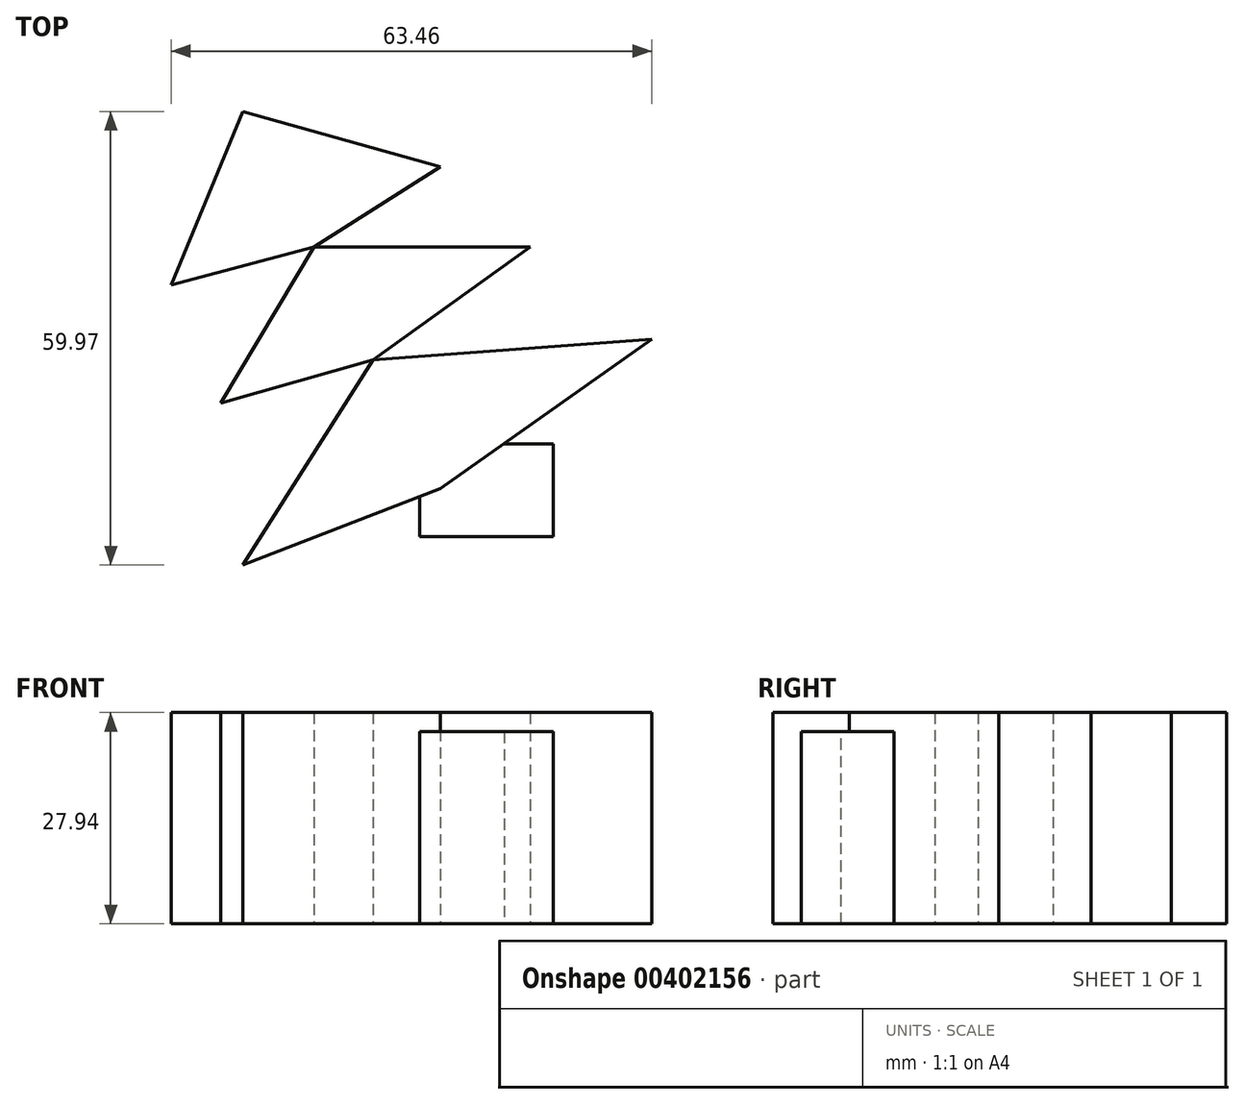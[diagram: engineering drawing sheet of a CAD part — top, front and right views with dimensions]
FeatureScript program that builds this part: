
annotation { "Feature Type Name" : "Feature", "Feature Type Description" : "" }
export const myFeature = defineFeature(function(context is Context, id is Id, definition is map)
    precondition{}
    {
        {
            var Q0;
            Q0=qCreatedBy(makeId("Top.planeOp"),FACE);
            var sketch = newSketch(context, id + "F0", { "sketchPlane" : qUnion([Q0])});
            skLineSegment(sketch, "E0", {"start": v(-37.95, 56.22) * mm, "end": v(-11.83, 6.33) * mm});
            skLineSegment(sketch, "E1", {"start": v(-37.95, 56.22) * mm, "end": v(-11.83, 48.93) * mm});
            skLineSegment(sketch, "E2", {"start": v(-28.56, 38.3) * mm, "end": v(-11.83, 48.93) * mm});
            skLineSegment(sketch, "E3", {"start": v(-28.56, 38.3) * mm, "end": v(0, 38.3) * mm});
            skLineSegment(sketch, "E4", {"start": v(-20.74, 23.35) * mm, "end": v(0, 38.3) * mm});
            skLineSegment(sketch, "E5", {"start": v(-20.74, 23.35) * mm, "end": v(16.07, 26.12) * mm});
            skLineSegment(sketch, "E6", {"start": v(-11.83, 6.33) * mm, "end": v(16.07, 26.12) * mm});
            skLineSegment(sketch, "E7", {"start": v(-37.95, 56.22) * mm, "end": v(-47.39, 33.26) * mm});
            skLineSegment(sketch, "E8", {"start": v(-47.39, 33.26) * mm, "end": v(-28.56, 38.3) * mm});
            skLineSegment(sketch, "E9", {"start": v(-28.56, 38.3) * mm, "end": v(-40.85, 17.65) * mm});
            skLineSegment(sketch, "E10", {"start": v(-40.85, 17.65) * mm, "end": v(-20.74, 23.35) * mm});
            skLineSegment(sketch, "E11", {"start": v(-20.74, 23.35) * mm, "end": v(-37.95, -3.75) * mm});
            skLineSegment(sketch, "E12", {"start": v(-37.95, -3.75) * mm, "end": v(-11.83, 6.33) * mm});
            skSolve(sketch);
        }
        {
            var Q0;
            Q0 = qSketchRegion(id + "F0", true);
            extrude(context, id + "F1", {"entities" : qUnion([Q0]), "depth" : 27.94 * mm});
        }
        {
            var Q0;
            Q0=qCreatedBy(makeId("Top.planeOp"),FACE);
            var sketch = newSketch(context, id + "F2", { "sketchPlane" : qUnion([Q0])});
            skLineSegment(sketch, "E13.bottom", {"start": v(-14.6, 0) * mm, "end": v(3.05, 0) * mm});
            skLineSegment(sketch, "E13.top", {"start": v(-14.6, 12.29) * mm, "end": v(3.05, 12.29) * mm});
            skLineSegment(sketch, "E13.left", {"start": v(-14.6, 0) * mm, "end": v(-14.6, 12.29) * mm});
            skLineSegment(sketch, "E13.right", {"start": v(3.05, 0) * mm, "end": v(3.05, 12.29) * mm});
            skSolve(sketch);
        }
        {
            var Q0;
            Q0 = qSketchRegion(id + "F2", true);
            extrude(context, id + "F3", {"entities" : qUnion([Q0]), "operationType" : NewBodyOperationType.ADD, "depth" : 25.4 * mm});
        }
    });
